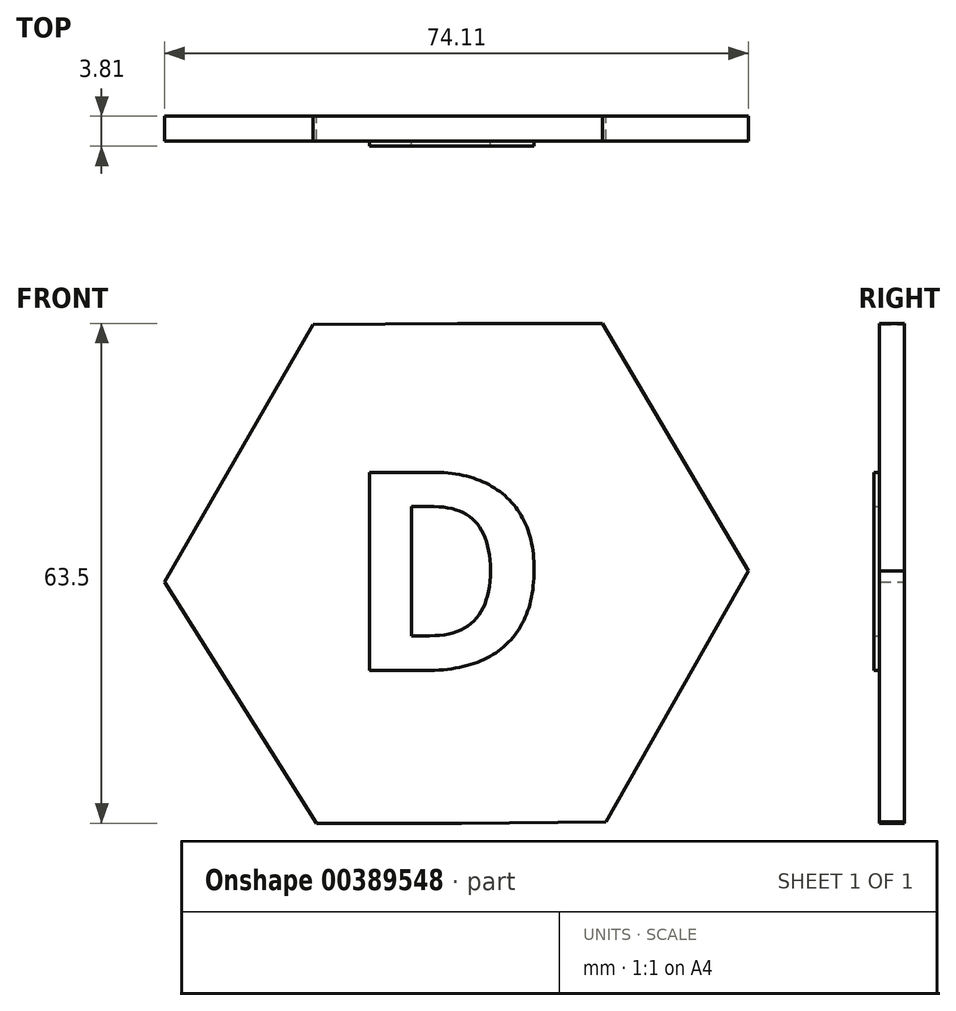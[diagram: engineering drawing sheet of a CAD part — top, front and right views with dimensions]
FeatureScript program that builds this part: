
annotation { "Feature Type Name" : "Feature", "Feature Type Description" : "" }
export const myFeature = defineFeature(function(context is Context, id is Id, definition is map)
    precondition{}
    {
        {
            var Q0;
            Q0=qCreatedBy(makeId("Front.planeOp"),FACE);
            var sketch = newSketch(context, id + "F0", { "sketchPlane" : qUnion([Q0])});
            skPoint(sketch, "E0.middle", {"position": v(0, 0) * mm});
            skLineSegment(sketch, "E1.0", {"start": v(18.07, 31.9) * mm, "end": v(36.66, 0.3) * mm});
            skLineSegment(sketch, "E1.1", {"start": v(36.66, 0.3) * mm, "end": v(18.6, -31.6) * mm});
            skLineSegment(sketch, "E1.2", {"start": v(18.6, -31.6) * mm, "end": v(-18.07, -31.9) * mm});
            skLineSegment(sketch, "E1.3", {"start": v(-18.07, -31.9) * mm, "end": v(-37.45, -1.08) * mm});
            skLineSegment(sketch, "E1.4", {"start": v(-37.45, -1.08) * mm, "end": v(-18.6, 31.6) * mm});
            skLineSegment(sketch, "E1.5", {"start": v(-18.6, 31.6) * mm, "end": v(18.07, 31.9) * mm});
            skLineSegment(sketch, "E2.bottom", {"start": v(38.1, 31.75) * mm, "end": v(-38.1, 31.75) * mm});
            skLineSegment(sketch, "E2.top", {"start": v(38.1, -31.75) * mm, "end": v(-38.1, -31.75) * mm});
            skLineSegment(sketch, "E2.left", {"start": v(38.1, 31.75) * mm, "end": v(38.1, -31.75) * mm});
            skLineSegment(sketch, "E2.right", {"start": v(-38.1, 31.75) * mm, "end": v(-38.1, -31.75) * mm});
            skSolve(sketch);
        }
        {
            var Q0;
            Q0=qCreatedBy(makeId("Front.planeOp"),FACE);
            var sketch = newSketch(context, id + "F1", { "sketchPlane" : qUnion([Q0])});
            skText(sketch, "E3", { "text": "D", "fontName": "OpenSans-Bold.ttf"});
            const initialGuessF1  = {"E3": [-0.01461, -0.01235, 1, 0, 0.0254]};
            skSetInitialGuess(sketch, initialGuessF1);
            skSolve(sketch);
        }
        {
            var Q0;
            Q0 = qSketchRegion(id + "F1", true);
            extrude(context, id + "F2", {"entities" : qUnion([Q0]), "depth" : 3.8 * mm});
        }
        {
            var Q0;
            {var subQ1=sQuery(id+"F0.wireOp",EDGE,"E1.1");Q0=makeQuery(id+"F0.imprint","IMPRINT",FACE,{"disambiguationData":[TD([[makeQuery(id+"F0.imprint","IMPRINT",EDGE,{"derivedFrom":subQ1}),-1.0]])]});}
            extrude(context, id + "F3", {"entities" : qUnion([Q0]), "operationType" : NewBodyOperationType.ADD, "depth" : 3.17 * mm});
        }
    });
